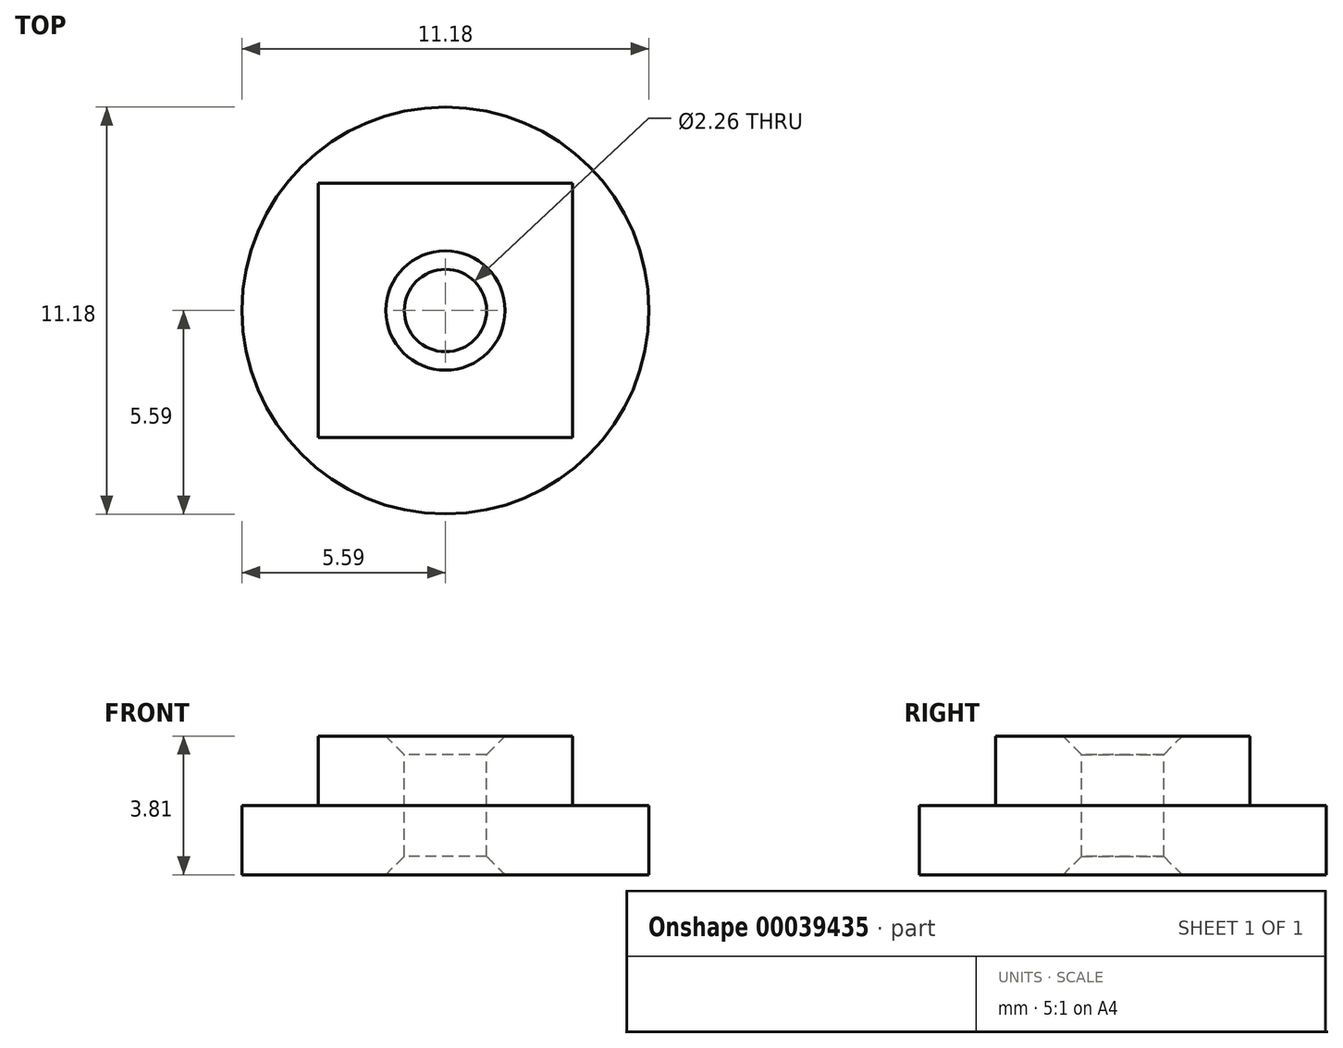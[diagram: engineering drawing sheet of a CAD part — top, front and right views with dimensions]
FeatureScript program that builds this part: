
annotation { "Feature Type Name" : "Feature", "Feature Type Description" : "" }
export const myFeature = defineFeature(function(context is Context, id is Id, definition is map)
    precondition{}
    {
        {
            var Q0;
            Q0=qCreatedBy(makeId("Top.planeOp"),FACE);
            var sketch = newSketch(context, id + "F0", { "sketchPlane" : qUnion([Q0])});
            skCircle(sketch, "E0", {"center": v(0, 0) * mm, "radius": 5.59 * mm});
            skSolve(sketch);
        }
        {
            var Q0;
            Q0=makeQuery(id+"F0.imprint","IMPRINT",FACE,{"disambiguationData":[TD([[makeQuery(id+"F0.imprint","IMPRINT",EDGE,{"derivedFrom":sQuery(id+"F0.wireOp",EDGE,"E0")}),1.0]])]});
            extrude(context, id + "F1", {"entities" : qUnion([Q0]), "depth" : 1.9 * mm});
        }
        {
            var Q0;
            Q0=makeQuery(id+"F1.opExtrude","CAP_FACE",FACE,{"disambiguationData":[OSD([sQuery(id+"F0.wireOp",EDGE,"E0")])],"isStart":false});
            var sketch = newSketch(context, id + "F2", { "sketchPlane" : qUnion([Q0])});
            skLineSegment(sketch, "E1.rect.bottom", {"start": v(-3.5, -3.5) * mm, "end": v(3.5, -3.5) * mm});
            skLineSegment(sketch, "E1.rect.top", {"start": v(-3.5, 3.5) * mm, "end": v(3.5, 3.5) * mm});
            skLineSegment(sketch, "E1.rect.left", {"start": v(-3.5, -3.5) * mm, "end": v(-3.5, 3.5) * mm});
            skLineSegment(sketch, "E1.rect.right", {"start": v(3.5, -3.5) * mm, "end": v(3.5, 3.5) * mm});
            skPoint(sketch, "E1.rect.middle", {"position": v(0, 0) * mm});
            skSolve(sketch);
        }
        {
            var Q0;
            Q0=makeQuery(id+"F2.imprint","IMPRINT",FACE,{"disambiguationData":[TD([[makeQuery(id+"F2.imprint","IMPRINT",EDGE,{"derivedFrom":sQuery(id+"F2.wireOp",EDGE,"E1.rect.bottom")}),1.0]])]});
            extrude(context, id + "F3", {"entities" : qUnion([Q0]), "operationType" : NewBodyOperationType.ADD, "depth" : 1.9 * mm});
        }
        {
            var Q0;
            Q0=makeQuery(id+"F3.opExtrude","CAP_FACE",FACE,{"disambiguationData":[OSD([sQuery(id+"F2.wireOp",EDGE,"E1.rect.bottom"),sQuery(id+"F2.wireOp",EDGE,"E1.rect.top"),sQuery(id+"F2.wireOp",EDGE,"E1.rect.left"),sQuery(id+"F2.wireOp",EDGE,"E1.rect.right")])],"isStart":false});
            var sketch = newSketch(context, id + "F4", { "sketchPlane" : qUnion([Q0])});
            skCircle(sketch, "E2", {"center": v(0, 0) * mm, "radius": 1.13 * mm});
            skSolve(sketch);
        }
        {
            var Q0;
            Q0=makeQuery(id+"F4.imprint","IMPRINT",FACE,{"disambiguationData":[TD([[makeQuery(id+"F4.imprint","IMPRINT",EDGE,{"derivedFrom":sQuery(id+"F4.wireOp",EDGE,"E2")}),1.0]])]});
            extrude(context, id + "F5", {"entities" : qUnion([Q0]), "operationType" : NewBodyOperationType.REMOVE, "endBound" : BoundingType.UP_TO_NEXT, "oppositeDirection" : true, "depth" : 25.4 * mm});
        }
        {
            var Q0;
            Q0=makeQuery(id+"F5.boolean.opBoolean","COPY",FACE,{"derivedFrom":makeQuery(id+"F5.opExtrude","SWEPT_FACE",FACE,{"disambiguationData":[OSD([sQuery(id+"F4.wireOp",EDGE,"E2")])]})});
            chamfer(context, id + "F6", {"entities" : qUnion([Q0]), "width" : 0.5 * mm, "tangentPropagation" : true});
        }
    });
